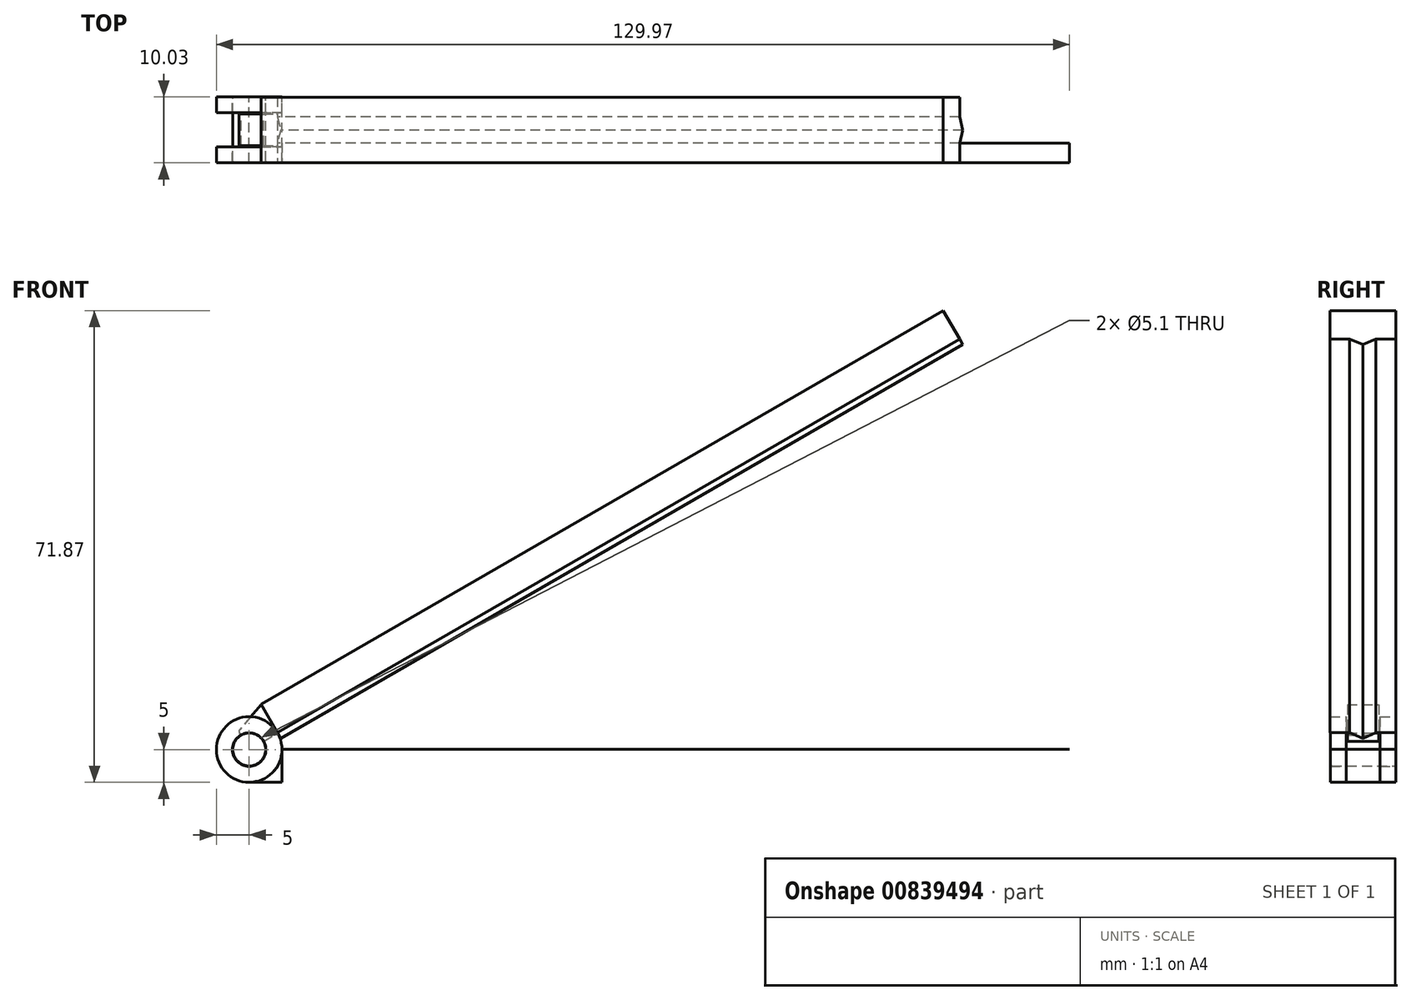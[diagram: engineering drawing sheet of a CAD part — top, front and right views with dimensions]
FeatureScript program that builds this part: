
annotation { "Feature Type Name" : "Feature", "Feature Type Description" : "" }
export const myFeature = defineFeature(function(context is Context, id is Id, definition is map)
    precondition{}
    {
        {
            assignVariable(context, id + "F0", {"name" : "len", "anyValue" : 1.33});
        }
        {
            var Q0;
            Q0=qCreatedBy(makeId("Front.planeOp"),FACE);
            var sketch = newSketch(context, id + "F1", { "sketchPlane" : qUnion([Q0])});
            skPoint(sketch, "E0.middle", {"position": v(0, 0) * mm});
            skLineSegment(sketch, "E1", {"start": v(0, -47.5) * mm, "end": v(0, -45) * mm});
            skLineSegment(sketch, "E2", {"start": v(0, -45) * mm, "end": v(0, 74.97) * mm});
            skLineSegment(sketch, "E3", {"start": v(-5, 74.97) * mm, "end": v(0, 74.97) * mm});
            skLineSegment(sketch, "E4", {"start": v(-5, -45) * mm, "end": v(-5, 74.97) * mm});
            skLineSegment(sketch, "E5", {"start": v(-5, -45) * mm, "end": v(-3.35, -49.75) * mm});
            skPoint(sketch, "E6.visualSharp", {"position": v(-3.26, -50) * mm});
            skCircle(sketch, "E7", {"center": v(0, -50) * mm, "radius": 2.5 * mm});
            skPoint(sketch, "E8.orphan", {"position": v(0, -48.75) * mm});
            skLineSegment(sketch, "E9", {"start": v(-2.5, -50) * mm, "end": v(-3, -50) * mm});
            skArc(sketch, "E10.filletArc", {"start": v(-3.35, -49.75) * mm, "mid": v(-3.22, -49.93) * mm, "end": v(-3, -50) * mm});
            skLineSegment(sketch, "E11", {"start": v(-5, -45) * mm, "end": v(0, -45) * mm});
            skSolve(sketch);
        }
        {
            var Q0;
            Q0=qCreatedBy(makeId("Top.planeOp"),FACE);
            var sketch = newSketch(context, id + "F2", { "sketchPlane" : qUnion([Q0])});
            skPoint(sketch, "E12.middle", {"position": v(-2.56, -0.03) * mm});
            skPoint(sketch, "E13.middle", {"position": v(0, 0) * mm});
            skPoint(sketch, "E14", {"position": v(0.94, -0.03) * mm});
            skLineSegment(sketch, "E15", {"start": v(-5.06, 4.97) * mm, "end": v(-0.06, 4.97) * mm});
            skLineSegment(sketch, "E16", {"start": v(-0.06, 4.97) * mm, "end": v(-0.06, 1.97) * mm});
            skLineSegment(sketch, "E17", {"start": v(-0.06, 1.97) * mm, "end": v(0.94, -0.03) * mm});
            skLineSegment(sketch, "E18", {"start": v(0.94, -0.03) * mm, "end": v(-0.06, -2.03) * mm});
            skLineSegment(sketch, "E19", {"start": v(-0.06, -2.03) * mm, "end": v(-0.06, -5.03) * mm});
            skLineSegment(sketch, "E20", {"start": v(-0.06, -5.03) * mm, "end": v(-5.06, -5.03) * mm});
            skLineSegment(sketch, "E21", {"start": v(-5.06, 4.97) * mm, "end": v(-5.06, -5.03) * mm});
            skLineSegment(sketch, "E22", {"start": v(-2.56, -10.75) * mm, "end": v(-2.56, 12.56) * mm, "construction": true});
            skPoint(sketch, "E22.endSnap0", {"position": v(-2.56, -5.03) * mm});
            skSolve(sketch);
        }
        {
            var Q0;
            Q0=makeQuery(id+"F2.imprint","IMPRINT",FACE,{"disambiguationData":[TD([[makeQuery(id+"F2.imprint","IMPRINT",EDGE,{"derivedFrom":sQuery(id+"F2.wireOp",EDGE,"E15")}),-1.0]])]});
            extrude(context, id + "F3", {"entities" : qUnion([Q0]), "depth" : ((getVariable(context, 'len') * 90) - 45) * mm, "offsetDistance" : 25 * mm, "hasSecondDirection" : true, "secondDirectionOppositeDirection" : true, "secondDirectionDepth" : 45 * mm});
        }
        {
            var Q0;
            {var subQ0=sQuery(id+"F1.wireOp",EDGE,"E7");var subQ1=makeQuery(id+"F1.imprint","INTERSECT",VERTEX,{"derivedFrom":[sQuery(id+"F1.wireOp",EDGE,"y2ifkrbQ-fr0k-EV40-WAJp-tS3gvMkOgowK"),subQ0]});Q0=makeQuery(id+"F1.imprint","IMPRINT",FACE,{"disambiguationData":[TD([[makeQuery(id+"F1.imprint","IMPRINT",EDGE,{"disambiguationData":[TD([[subQ1,1.0]])],"derivedFrom":subQ0}),1.0]])]});}
            extrude(context, id + "F4", {"entities" : qUnion([Q0]), "operationType" : NewBodyOperationType.ADD, "depth" : 5 * mm, "offsetDistance" : 25 * mm, "hasSecondDirection" : true, "secondDirectionOppositeDirection" : true, "secondDirectionDepth" : 5 * mm});
        }
        {
            var Q0;
            {var subQ2=sQuery(id+"F1.wireOp",EDGE,"E1");Q0=makeQuery(id+"F1.imprint","IMPRINT",FACE,{"disambiguationData":[TD([[makeQuery(id+"F1.imprint","IMPRINT",EDGE,{"derivedFrom":subQ2}),1.0]])]});}
            extrude(context, id + "F5", {"entities" : qUnion([Q0]), "depth" : 2.4 * mm, "offsetDistance" : 25 * mm, "hasSecondDirection" : true, "secondDirectionOppositeDirection" : true, "secondDirectionDepth" : 2.4 * mm});
        }
        {
            var Q0;
            Q0=makeQuery(id+"F4.opExtrude","CAP_FACE",FACE,{"disambiguationData":[OSD([sQuery(id+"F1.wireOp",EDGE,"E7")])],"isStart":false});
            var Q1;
            Q1=makeQuery(id+"F4.opExtrude","CAP_FACE",FACE,{"disambiguationData":[OSD([sQuery(id+"F1.wireOp",EDGE,"E7")])],"isStart":true});
            fillet(context, id + "F6", {"entities" : qUnion([Q0, Q1]), "radius" : .25 * mm, "tangentPropagation" : true, "allowEdgeOverflow" : false});
        }
        {
            var Q0;
            Q0=makeQuery(id+"F3.opExtrude","SWEPT_FACE",FACE,{"disambiguationData":[OSD([sQuery(id+"F2.wireOp",EDGE,"ip5yjFWY-FGmT-liJ9-8fW3-jcPs83EoBgNt")])]});
            var Q1;
            Q1=qCreatedBy(makeId("Front.planeOp"),FACE);
            cPlane(context, id + "F7", {"entities" : qUnion([Q0, Q1]), "cplaneType" : CPlaneType.OFFSET, "offset" : 0 * mm, "width" : 150 * mm, "height" : 150 * mm});
        }
        {
            var Q0;
            Q0=qCreatedBy(id+"F7.planeOp",FACE);
            var sketch = newSketch(context, id + "F8", { "sketchPlane" : qUnion([Q0])});
            skPoint(sketch, "E23", {"position": v(0, -50) * mm});
            skCircle(sketch, "E24", {"center": v(0, -50) * mm, "radius": 124.97 * mm, "construction": true});
            skLineSegment(sketch, "E25.right", {"start": v(5, -50) * mm, "end": v(5, -55) * mm});
            skLineSegment(sketch, "E26", {"start": v(5, -50) * mm, "end": v(124.97, -50) * mm});
            skLineSegment(sketch, "E27", {"start": v(124.97, -55) * mm, "end": v(125.37, -55) * mm});
            skLineSegment(sketch, "E28", {"start": v(125.37, -43.8) * mm, "end": v(122.57, -43.8) * mm});
            skLineSegment(sketch, "E29", {"start": v(127.37, -55) * mm, "end": v(125.37, -55) * mm});
            skLineSegment(sketch, "E30", {"start": v(127.37, -37.65) * mm, "end": v(127.37, -55) * mm});
            skLineSegment(sketch, "E31", {"start": v(125.37, -43.8) * mm, "end": v(125.37, -53.5) * mm});
            skLineSegment(sketch, "E32", {"start": v(124.97, -50) * mm, "end": v(125.37, -50) * mm});
            skLineSegment(sketch, "E33", {"start": v(5, -50) * mm, "end": v(5, -32.35) * mm, "construction": true});
            skLineSegment(sketch, "E34", {"start": v(122.57, -43.8) * mm, "end": v(126.7, -37.45) * mm});
            skCircle(sketch, "E35", {"center": v(0, -50) * mm, "radius": 5 * mm});
            skCircle(sketch, "E36", {"center": v(0, -50) * mm, "radius": 3 * mm});
            skLineSegment(sketch, "E37", {"start": v(-3, -50) * mm, "end": v(-5, -50) * mm});
            skLineSegment(sketch, "E38", {"start": v(0, -47) * mm, "end": v(0, -45) * mm});
            skLineSegment(sketch, "E39", {"start": v(124.97, -55) * mm, "end": v(0, -55) * mm});
            skPoint(sketch, "E40.visualSharp", {"position": v(127.37, -36.4) * mm});
            skArc(sketch, "E40.filletArc", {"start": v(127.37, -37.65) * mm, "mid": v(127.1, -37.3) * mm, "end": v(126.7, -37.45) * mm});
            skLineSegment(sketch, "E41", {"start": v(125.37, -53.5) * mm, "end": v(117.37, -53.5) * mm});
            skLineSegment(sketch, "E42", {"start": v(117.37, -53.1) * mm, "end": v(117.37, -53.5) * mm});
            skLineSegment(sketch, "E43", {"start": v(117.37, -53.1) * mm, "end": v(124.93, -53.1) * mm});
            skLineSegment(sketch, "E44", {"start": v(124.93, -53.1) * mm, "end": v(124.97, -50) * mm});
            skLineSegment(sketch, "E45", {"start": v(117.37, -53.5) * mm, "end": v(117.37, -55) * mm});
            skSolve(sketch);
        }
        {
            var Q0;
            Q0=qCreatedBy(makeId("Right.planeOp"),FACE);
            var sketch = newSketch(context, id + "F9", { "sketchPlane" : qUnion([Q0])});
            skLineSegment(sketch, "E46", {"start": v(0, -59.14) * mm, "end": v(0, -40.5) * mm, "construction": true});
            skPoint(sketch, "E47", {"position": v(-5, -50.02) * mm});
            skLineSegment(sketch, "E48", {"start": v(-5, -45.02) * mm, "end": v(-2.59, -45.02) * mm});
            skLineSegment(sketch, "E49", {"start": v(-2.59, -50.02) * mm, "end": v(-5, -50.02) * mm, "construction": true});
            skLineSegment(sketch, "E50.MirrorCS", {"start": v(5, -45.02) * mm, "end": v(2.59, -45.02) * mm});
            skLineSegment(sketch, "E51.MirrorCS", {"start": v(5, -50.02) * mm, "end": v(5, -45.02) * mm, "construction": true});
            skLineSegment(sketch, "E52.MirrorCS", {"start": v(2.59, -50.02) * mm, "end": v(5, -50.02) * mm, "construction": true});
            skLineSegment(sketch, "E53", {"start": v(6.96, -50.02) * mm, "end": v(-6.61, -50.02) * mm, "construction": true});
            skLineSegment(sketch, "E54", {"start": v(-5.97, -50.02) * mm, "end": v(-5.97, -47.47) * mm, "construction": true});
            skLineSegment(sketch, "E55", {"start": v(-5, -45.02) * mm, "end": v(-5, -47.47) * mm});
            skLineSegment(sketch, "E56", {"start": v(-5, -47.47) * mm, "end": v(-2.59, -47.47) * mm});
            skLineSegment(sketch, "E57", {"start": v(-2.59, -47.47) * mm, "end": v(-2.59, -45.02) * mm});
            skLineSegment(sketch, "E58.MirrorCS", {"start": v(5, -45.02) * mm, "end": v(5, -47.47) * mm});
            skLineSegment(sketch, "E59.MirrorCS", {"start": v(2.59, -47.47) * mm, "end": v(2.59, -45.02) * mm});
            skLineSegment(sketch, "E60.MirrorCS", {"start": v(5, -47.47) * mm, "end": v(2.59, -47.47) * mm});
            skSolve(sketch);
        }
        {
            var Q0;
            Q0 = qSketchRegion(id + "F9", true);
            var Q1;
            Q1=sQuery(id+"F9.wireOp",EDGE,"E53");
            revolve(context, id + "F10", {"surfaceOperationType" : NewSurfaceOperationType.NEW, "entities" : qUnion([Q0]), "axis" : qUnion([Q1]), "revolveType" : RevolveType.FULL});
        }
        {
            var Q0;
            {var subQ4=sQuery(id+"F8.wireOp",EDGE,"E25.right");Q0=makeQuery(id+"F8.imprint","IMPRINT",FACE,{"disambiguationData":[TD([[makeQuery(id+"F8.imprint","IMPRINT",EDGE,{"derivedFrom":subQ4}),-1.0]])]});}
            extrude(context, id + "F11", {"entities" : qUnion([Q0]), "depth" : 5 * mm, "offsetDistance" : 25 * mm, "hasSecondDirection" : true, "secondDirectionOppositeDirection" : true, "secondDirectionDepth" : 5 * mm});
        }
        {
            var Q0;
            Q0=makeQuery(id+"F11.opExtrude","SWEPT_FACE",FACE,{"disambiguationData":[OSD([sQuery(id+"F8.wireOp",EDGE,"E25.right")])]});
            var Q1;
            Q1=qBodyType(qCreatedBy(id+"F13",EDGE),BodyType.WIRE);
            cPlane(context, id + "F12", {"entities" : qUnion([Q0, Q1]), "cplaneType" : CPlaneType.OFFSET, "offset" : 0 * mm, "width" : 150 * mm, "height" : 150 * mm});
        }
        {
            var Q0;
            Q0=qCreatedBy(id+"F12.planeOp",FACE);
            var sketch = newSketch(context, id + "F13", { "sketchPlane" : qUnion([Q0])});
            skPoint(sketch, "E61", {"position": v(0, -52.5) * mm});
            skLineSegment(sketch, "E62", {"start": v(-7.37, -52.5) * mm, "end": v(6.54, -52.5) * mm, "construction": true});
            skPoint(sketch, "E63.middle", {"position": v(0, -50) * mm});
            skLineSegment(sketch, "E64", {"start": v(0, -55) * mm, "end": v(0, -48.4) * mm, "construction": true});
            skPoint(sketch, "E65", {"position": v(-5, -50) * mm});
            skPoint(sketch, "E66", {"position": v(-2, -50) * mm});
            skPoint(sketch, "E67", {"position": v(2, -50) * mm});
            skPoint(sketch, "E68", {"position": v(5, -50) * mm});
            skLineSegment(sketch, "E69", {"start": v(-5, -50) * mm, "end": v(-5, -50) * mm});
            skLineSegment(sketch, "E70", {"start": v(-5, -50) * mm, "end": v(-2, -50) * mm});
            skLineSegment(sketch, "E71", {"start": v(2, -50) * mm, "end": v(5, -50) * mm});
            skLineSegment(sketch, "E72", {"start": v(5, -50) * mm, "end": v(5, -50) * mm});
            skLineSegment(sketch, "E73", {"start": v(5, -50) * mm, "end": v(2, -50) * mm});
            skLineSegment(sketch, "E74", {"start": v(3.05, -50) * mm, "end": v(3.05, -52) * mm, "construction": true});
            skPoint(sketch, "E75", {"position": v(0, -52) * mm});
            skLineSegment(sketch, "E76", {"start": v(2, -50) * mm, "end": v(0, -52) * mm});
            skLineSegment(sketch, "E77", {"start": v(-2, -50) * mm, "end": v(0, -52) * mm});
            skLineSegment(sketch, "E78", {"start": v(5, -50) * mm, "end": v(5, -55) * mm});
            skLineSegment(sketch, "E79", {"start": v(5, -55) * mm, "end": v(-5, -55) * mm});
            skLineSegment(sketch, "E80", {"start": v(-5, -55) * mm, "end": v(-5, -50) * mm});
            skLineSegment(sketch, "E81.trimOffspring", {"start": v(-2, -50) * mm, "end": v(-5, -50) * mm});
            skSolve(sketch);
        }
        {
            var Q0;
            {var subQ1=sQuery(id+"F13.wireOp",EDGE,"E70");Q0=makeQuery(id+"F13.imprint","IMPRINT",FACE,{"disambiguationData":[TD([[makeQuery(id+"F13.imprint","IMPRINT",EDGE,{"derivedFrom":subQ1}),-1.0]])]});}
            extrude(context, id + "F14", {"entities" : qUnion([Q0]), "depth" : (getVariable(context, 'len') * 90) * mm, "offsetDistance" : 25 * mm});
        }
        {
            var Q0;
            {var subQ1=sQuery(id+"F8.wireOp",EDGE,"E32");Q0=makeQuery(id+"F8.imprint","IMPRINT",FACE,{"disambiguationData":[TD([[makeQuery(id+"F8.imprint","IMPRINT",EDGE,{"derivedFrom":subQ1}),-1.0]])]});}
            extrude(context, id + "F15", {"entities" : qUnion([Q0]), "operationType" : NewBodyOperationType.REMOVE, "depth" : 5 * mm, "offsetDistance" : 25 * mm, "hasSecondDirection" : true, "secondDirectionOppositeDirection" : true, "secondDirectionDepth" : 5 * mm});
        }
        {
            var Q0;
            Q0=makeQuery(id+"F3.opExtrude","SWEPT_BODY",BODY,{"disambiguationData":[OSD([sQuery(id+"F2.wireOp",EDGE,"E15"),sQuery(id+"F2.wireOp",EDGE,"E16"),sQuery(id+"F2.wireOp",EDGE,"E17"),sQuery(id+"F2.wireOp",EDGE,"E18"),sQuery(id+"F2.wireOp",EDGE,"E19"),sQuery(id+"F2.wireOp",EDGE,"E20"),sQuery(id+"F2.wireOp",EDGE,"E21")])]});
            var Q1;
            Q1=makeQuery(id+"F5.opExtrude","SWEPT_BODY",BODY,{"disambiguationData":[OSD([sQuery(id+"F1.wireOp",EDGE,"E1"),sQuery(id+"F1.wireOp",EDGE,"E5"),sQuery(id+"F1.wireOp",EDGE,"E7"),sQuery(id+"F1.wireOp",EDGE,"E9"),sQuery(id+"F1.wireOp",EDGE,"E10.filletArc"),sQuery(id+"F1.wireOp",EDGE,"E11")])]});
            var Q2;
            Q2=makeQuery(id+"F4.opExtrude","SWEPT_BODY",BODY,{"disambiguationData":[OSD([sQuery(id+"F1.wireOp",EDGE,"E7")])]});
            var Q3;
            Q3=sQuery(id+"F9.wireOp",EDGE,"E53");
            transform(context, id + "F16", {"entities" : qUnion([Q0, Q1, Q2]), "transformType" : TransformType.ROTATION, "transformAxis" : qUnion([Q3]), "angle" : 60 * degree, "oppositeDirection" : true, "makeCopy" : false});
        }
    });
